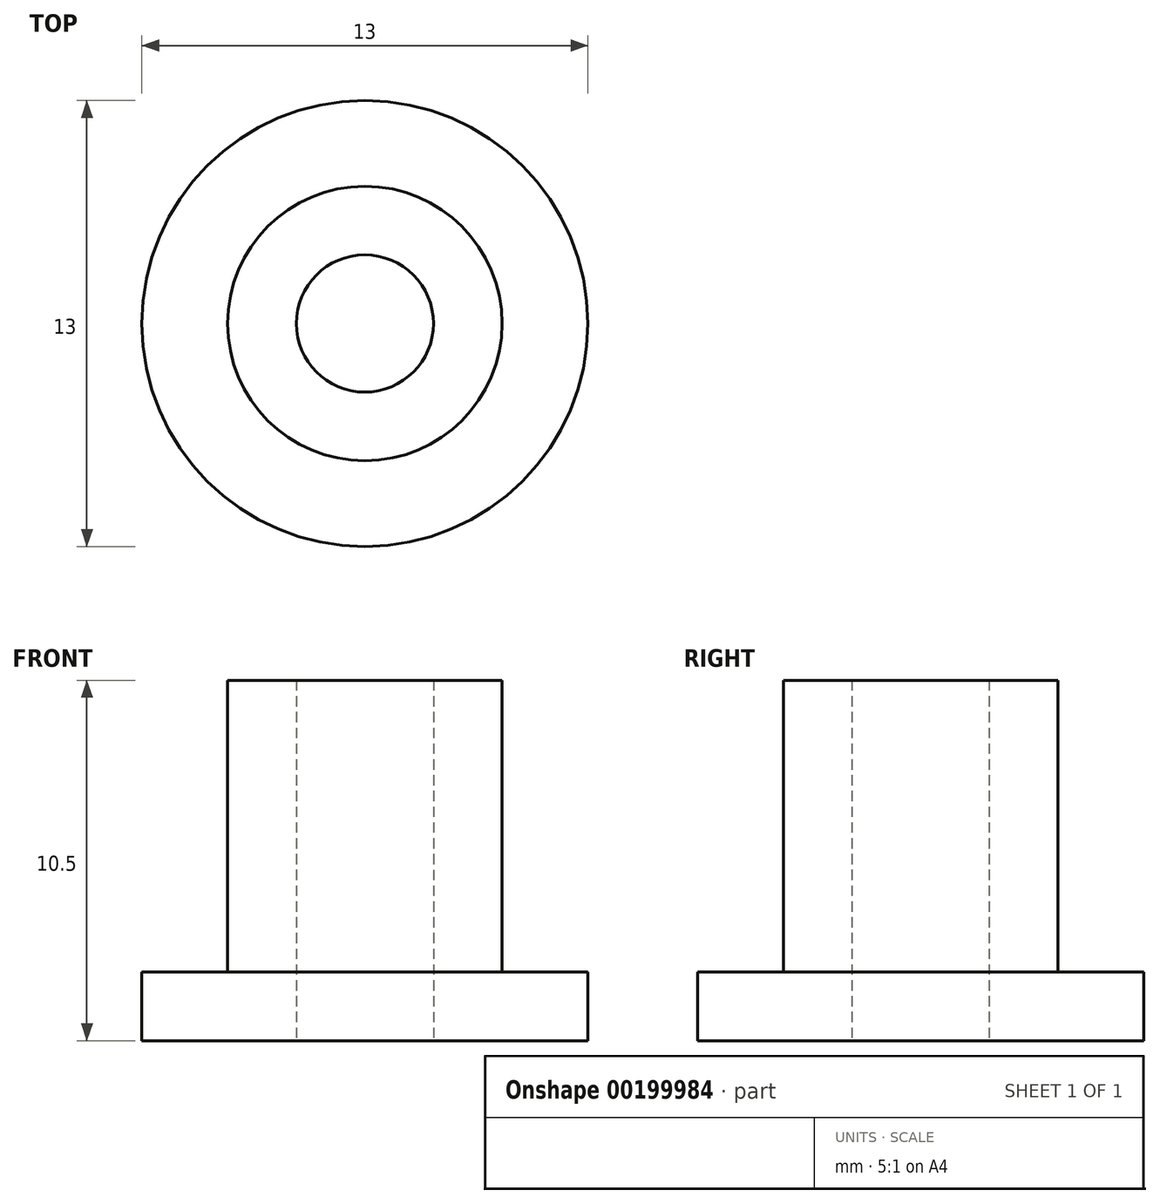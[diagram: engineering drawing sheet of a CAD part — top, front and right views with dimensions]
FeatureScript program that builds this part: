
annotation { "Feature Type Name" : "Feature", "Feature Type Description" : "" }
export const myFeature = defineFeature(function(context is Context, id is Id, definition is map)
    precondition{}
    {
        {
            var Q0;
            Q0=qCreatedBy(makeId("Top.planeOp"),FACE);
            var sketch = newSketch(context, id + "F0", { "sketchPlane" : qUnion([Q0])});
            skCircle(sketch, "E0", {"center": v(0, 0) * mm, "radius": 2 * mm});
            skCircle(sketch, "E1", {"center": v(0, 0) * mm, "radius": 4 * mm});
            skSolve(sketch);
        }
        {
            var Q0;
            Q0=makeQuery(id+"F0.imprint","IMPRINT",FACE,{"disambiguationData":[TD([[makeQuery(id+"F0.imprint","IMPRINT",EDGE,{"derivedFrom":sQuery(id+"F0.wireOp",EDGE,"E0")}),-1.0]])]});
            extrude(context, id + "F1", {"entities" : qUnion([Q0]), "depth" : 8.5 * mm});
        }
        {
            var Q0;
            Q0=qCreatedBy(makeId("Top.planeOp"),FACE);
            var sketch = newSketch(context, id + "F2", { "sketchPlane" : qUnion([Q0])});
            skCircle(sketch, "E2", {"center": v(0, 0) * mm, "radius": 6.5 * mm});
            skSolve(sketch);
        }
        {
            var Q0;
            Q0=makeQuery(id+"F2.imprint","IMPRINT",FACE,{"disambiguationData":[TD([[makeQuery(id+"F2.imprint","IMPRINT",EDGE,{"derivedFrom":sQuery(id+"F2.wireOp",EDGE,"E2")}),1.0]])]});
            extrude(context, id + "F3", {"entities" : qUnion([Q0]), "operationType" : NewBodyOperationType.ADD, "oppositeDirection" : true, "depth" : 2 * mm});
        }
        {
            var Q0;
            Q0=makeQuery(id+"F0.imprint","IMPRINT",FACE,{"disambiguationData":[TD([[makeQuery(id+"F0.imprint","IMPRINT",EDGE,{"derivedFrom":sQuery(id+"F0.wireOp",EDGE,"E0")}),1.0]])]});
            var Q1;
            Q1=sQuery(id+"F0.wireOp",EDGE,"E0");
            extrude(context, id + "F4", {"entities" : qUnion([Q0]), "operationType" : NewBodyOperationType.REMOVE, "surfaceEntities" : qUnion([Q1]), "oppositeDirection" : true, "depth" : 3 * mm});
        }
    });
